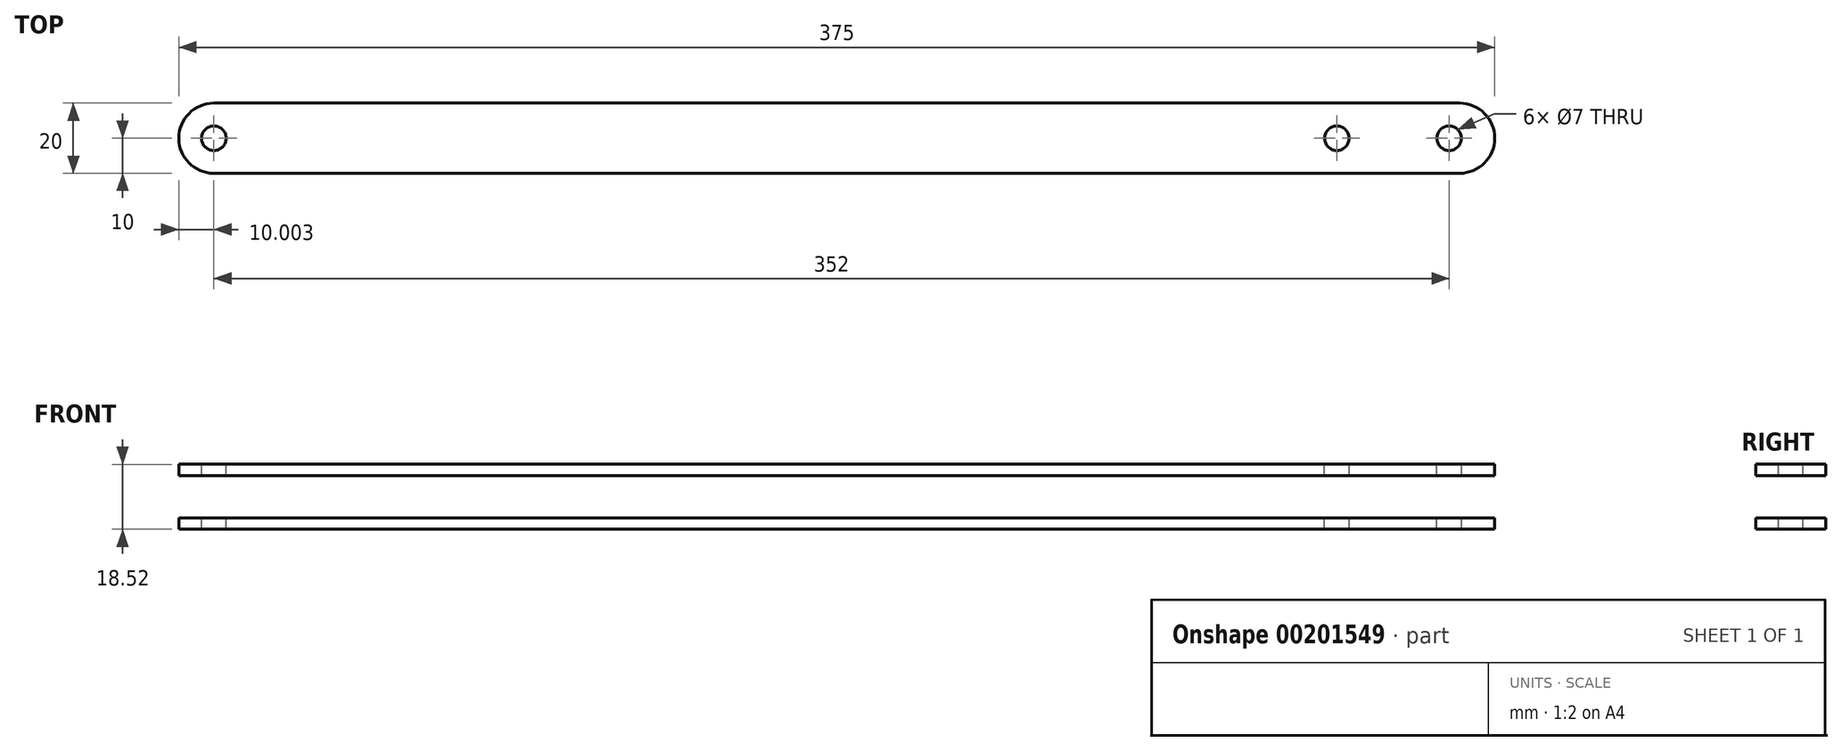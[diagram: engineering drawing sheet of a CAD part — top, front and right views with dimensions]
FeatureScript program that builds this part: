
annotation { "Feature Type Name" : "Feature", "Feature Type Description" : "" }
export const myFeature = defineFeature(function(context is Context, id is Id, definition is map)
    precondition{}
    {
        {
            var Q0;
            Q0=qCreatedBy(makeId("Front.planeOp"),FACE);
            var sketch = newSketch(context, id + "F0", { "sketchPlane" : qUnion([Q0])});
            skLineSegment(sketch, "E0", {"start": v(-44.34, -8.72) * mm, "end": v(330.66, -8.72) * mm});
            skLineSegment(sketch, "E1", {"start": v(330.66, -5.46) * mm, "end": v(-44.34, -5.46) * mm});
            skLineSegment(sketch, "E2", {"start": v(330.66, -5.46) * mm, "end": v(330.66, -8.72) * mm});
            skLineSegment(sketch, "E3.bottom", {"start": v(-44.34, 6.54) * mm, "end": v(330.66, 6.54) * mm});
            skLineSegment(sketch, "E3.top", {"start": v(-44.34, 9.8) * mm, "end": v(330.66, 9.8) * mm});
            skLineSegment(sketch, "E3.right", {"start": v(330.66, 6.54) * mm, "end": v(330.66, 9.8) * mm});
            skLineSegment(sketch, "E4", {"start": v(-44.34, 9.8) * mm, "end": v(-44.34, 6.54) * mm});
            skLineSegment(sketch, "E5", {"start": v(-44.34, -5.46) * mm, "end": v(-44.34, -8.72) * mm});
            skSolve(sketch);
        }
        {
            var Q0;
            Q0=makeQuery(id+"F0.imprint","IMPRINT",FACE,{"disambiguationData":[TD([[makeQuery(id+"F0.imprint","IMPRINT",EDGE,{"derivedFrom":sQuery(id+"F0.wireOp",EDGE,"E0")}),1.0]])]});
            var Q1;
            Q1=makeQuery(id+"F0.imprint","IMPRINT",FACE,{"disambiguationData":[TD([[makeQuery(id+"F0.imprint","IMPRINT",EDGE,{"derivedFrom":sQuery(id+"F0.wireOp",EDGE,"E3.bottom")}),1.0]])]});
            extrude(context, id + "F1", {"entities" : qUnion([Q0, Q1]), "depth" : 20 * mm, "offsetDistance" : 25 * mm});
        }
        {
            var Q0;
            Q0=makeQuery(id+"F1.opExtrude","CAP_EDGE",EDGE,{"disambiguationData":[OSD([sQuery(id+"F0.wireOp",EDGE,"E3.right")])],"isStart":false});
            var Q1;
            Q1=makeQuery(id+"F1.opExtrude","CAP_EDGE",EDGE,{"disambiguationData":[OSD([sQuery(id+"F0.wireOp",EDGE,"E3.right")])],"isStart":true});
            var Q2;
            Q2=makeQuery(id+"F1.opExtrude","CAP_EDGE",EDGE,{"disambiguationData":[OSD([sQuery(id+"F0.wireOp",EDGE,"E2")])],"isStart":false});
            var Q3;
            Q3=makeQuery(id+"F1.opExtrude","CAP_EDGE",EDGE,{"disambiguationData":[OSD([sQuery(id+"F0.wireOp",EDGE,"E2")])],"isStart":true});
            var Q4;
            Q4=makeQuery(id+"F1.opExtrude","CAP_EDGE",EDGE,{"disambiguationData":[OSD([sQuery(id+"F0.wireOp",EDGE,"E3.left")])],"isStart":false});
            var Q5;
            Q5=makeQuery(id+"F1.opExtrude","CAP_EDGE",EDGE,{"disambiguationData":[OSD([sQuery(id+"F0.wireOp",EDGE,"E3.left")])],"isStart":true});
            var Q6;
            Q6=makeQuery(id+"F1.opExtrude","CAP_EDGE",EDGE,{"disambiguationData":[OSD([sQuery(id+"F0.wireOp",EDGE,"DgdLVRv8-ghu1-qQor-eS9p-4OY0FDmrB7ef")])],"isStart":true});
            var Q7;
            Q7=makeQuery(id+"F1.opExtrude","CAP_EDGE",EDGE,{"disambiguationData":[OSD([sQuery(id+"F0.wireOp",EDGE,"DgdLVRv8-ghu1-qQor-eS9p-4OY0FDmrB7ef")])],"isStart":false});
            var Q8;
            Q8=makeQuery(id+"F1.opExtrude","CAP_EDGE",EDGE,{"disambiguationData":[OSD([sQuery(id+"F0.wireOp",EDGE,"E4")])],"isStart":true});
            var Q9;
            Q9=makeQuery(id+"F1.opExtrude","CAP_EDGE",EDGE,{"disambiguationData":[OSD([sQuery(id+"F0.wireOp",EDGE,"E4")])],"isStart":false});
            var Q10;
            Q10=makeQuery(id+"F1.opExtrude","CAP_EDGE",EDGE,{"disambiguationData":[OSD([sQuery(id+"F0.wireOp",EDGE,"E5")])],"isStart":true});
            var Q11;
            Q11=makeQuery(id+"F1.opExtrude","CAP_EDGE",EDGE,{"disambiguationData":[OSD([sQuery(id+"F0.wireOp",EDGE,"E5")])],"isStart":false});
            fillet(context, id + "F2", {"entities" : qUnion([Q0, Q1, Q2, Q3, Q4, Q5, Q6, Q7, Q8, Q9, Q10, Q11]), "radius" : 10 * mm, "tangentPropagation" : true, "allowEdgeOverflow" : false});
        }
        {
            var Q0;
            Q0=makeQuery(id+"F1.opExtrude","SWEPT_FACE",FACE,{"disambiguationData":[OSD([sQuery(id+"F0.wireOp",EDGE,"E3.top")])]});
            var sketch = newSketch(context, id + "F3", { "sketchPlane" : qUnion([Q0])});
            skCircle(sketch, "E6", {"center": v(317.66, -10) * mm, "radius": 3.5 * mm});
            skCircle(sketch, "E7", {"center": v(285.66, -10) * mm, "radius": 3.5 * mm});
            skLineSegment(sketch, "E8", {"start": v(-44.34, -10) * mm, "end": v(330.66, -10) * mm, "construction": true});
            skCircle(sketch, "E9", {"center": v(-34.34, -10) * mm, "radius": 3.5 * mm});
            skSolve(sketch);
        }
        {
            var Q0;
            Q0=makeQuery(id+"F3.imprint","IMPRINT",FACE,{"disambiguationData":[TD([[makeQuery(id+"F3.imprint","IMPRINT",EDGE,{"derivedFrom":sQuery(id+"F3.wireOp",EDGE,"Tt5ugM9U-maDa-Bape-ksyI-QPuQc9gj2rs1")}),1.0]])]});
            var Q1;
            Q1=makeQuery(id+"F3.imprint","IMPRINT",FACE,{"disambiguationData":[TD([[makeQuery(id+"F3.imprint","IMPRINT",EDGE,{"derivedFrom":sQuery(id+"F3.wireOp",EDGE,"E6")}),1.0]])]});
            var Q2;
            Q2=makeQuery(id+"F3.imprint","IMPRINT",FACE,{"disambiguationData":[TD([[makeQuery(id+"F3.imprint","IMPRINT",EDGE,{"derivedFrom":sQuery(id+"F3.wireOp",EDGE,"E7")}),1.0]])]});
            var Q3;
            Q3=makeQuery(id+"F3.imprint","IMPRINT",FACE,{"disambiguationData":[TD([[makeQuery(id+"F3.imprint","IMPRINT",EDGE,{"derivedFrom":sQuery(id+"F3.wireOp",EDGE,"E9")}),1.0]])]});
            extrude(context, id + "F4", {"entities" : qUnion([Q0, Q1, Q2, Q3]), "operationType" : NewBodyOperationType.REMOVE, "oppositeDirection" : true, "depth" : 25 * mm, "offsetDistance" : 25 * mm});
        }
    });
